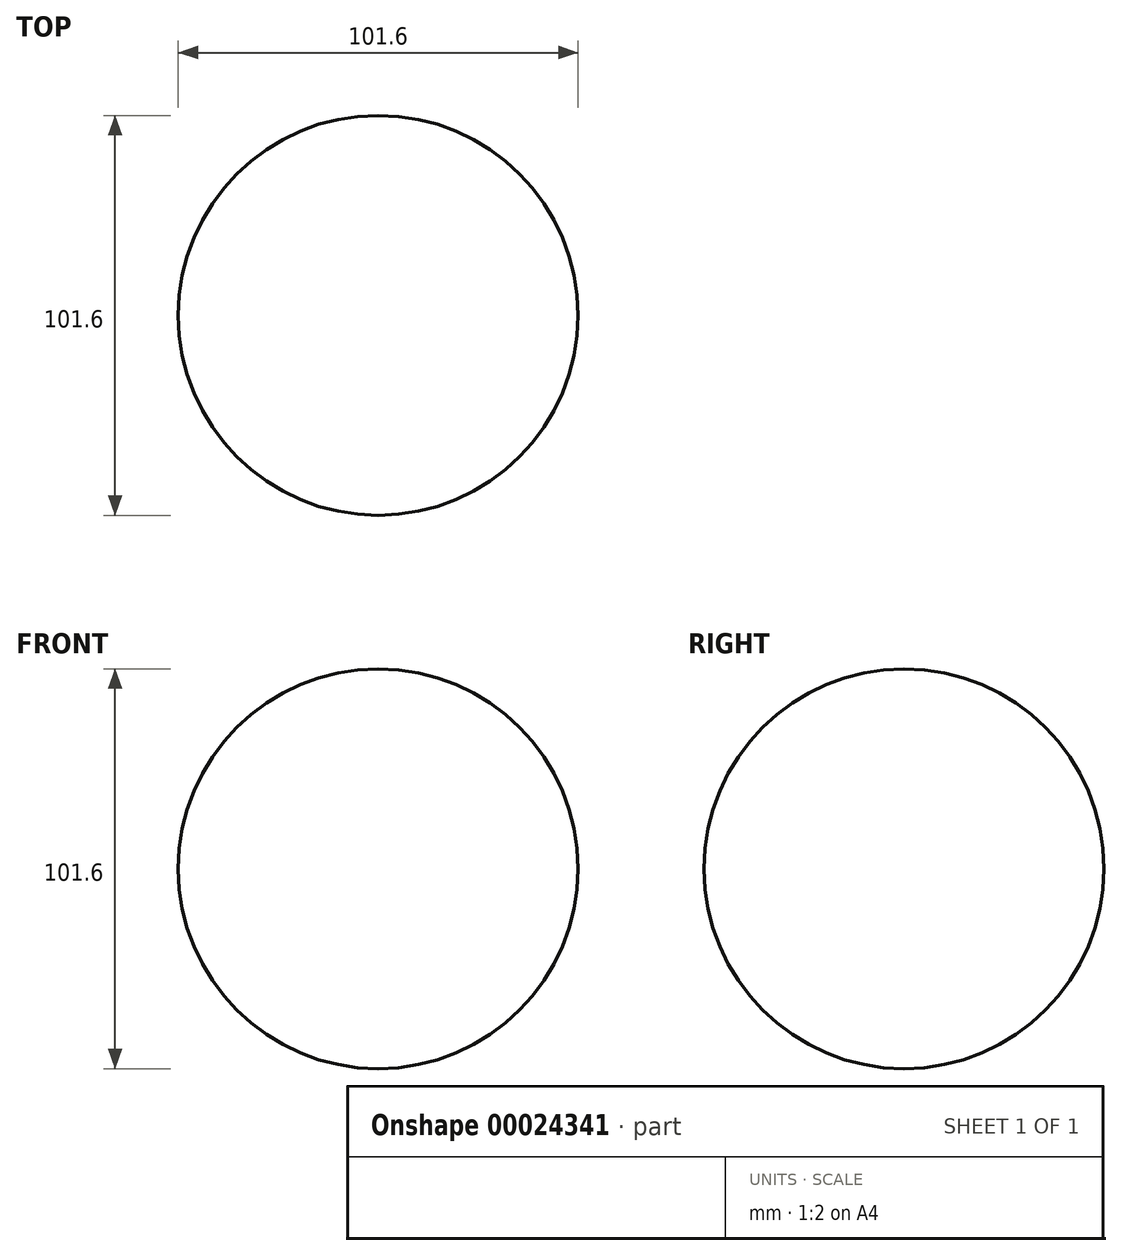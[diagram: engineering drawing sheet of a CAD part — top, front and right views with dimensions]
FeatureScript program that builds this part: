
annotation { "Feature Type Name" : "Feature", "Feature Type Description" : "" }
export const myFeature = defineFeature(function(context is Context, id is Id, definition is map)
    precondition{}
    {
        {
            var Q0;
            Q0=qCreatedBy(makeId("Top.planeOp"),FACE);
            var sketch = newSketch(context, id + "F0", { "sketchPlane" : qUnion([Q0])});
            skCircle(sketch, "E0", {"center": v(0, 0) * mm, "radius": 50.8 * mm});
            skLineSegment(sketch, "E1", {"start": v(-50.8, 0) * mm, "end": v(50.8, 0) * mm});
            skLineSegment(sketch, "E2", {"start": v(50.8, 0) * mm, "end": v(86.5, 0) * mm});
            skSolve(sketch);
        }
        {
            var Q0;
            {var subQ0=sQuery(id+"F0.wireOp",EDGE,"E1");Q0=makeQuery(id+"F0.imprint","IMPRINT",FACE,{"disambiguationData":[TD([[makeQuery(id+"F0.imprint","IMPRINT",EDGE,{"derivedFrom":subQ0}),1.0]])]});}
            var Q1;
            Q1=sQuery(id+"F0.wireOp",EDGE,"E2");
            revolve(context, id + "F1", {"entities" : qUnion([Q0]), "axis" : qUnion([Q1]), "revolveType" : RevolveType.FULL});
        }
    });
